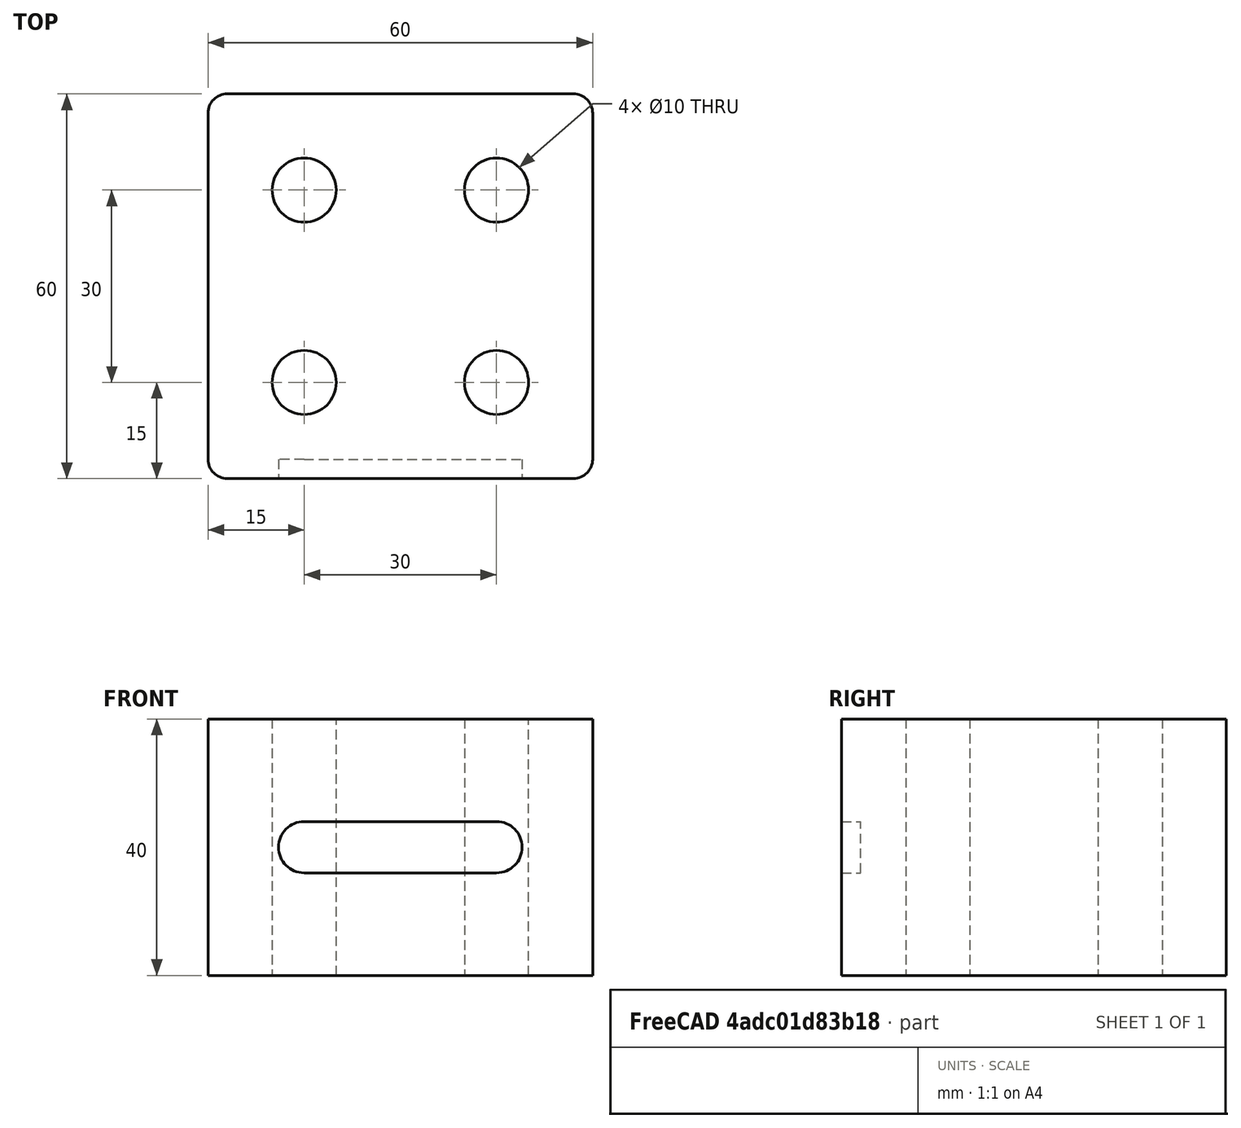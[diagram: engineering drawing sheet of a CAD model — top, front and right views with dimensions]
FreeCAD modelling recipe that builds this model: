
FCSTD DOCUMENT  (FreeCAD 1.0R39319 (Git))
Label: Assignment_10.1_Block(2d_Drawing)
License: All rights reserved
LicenseURL: https://en.wikipedia.org/wiki/All_rights_reserved
objects: TechDraw::DrawViewDimension×9, TechDraw::DrawViewAnnotation×5, TechDraw::DrawProjGroupItem×4, Sketcher::SketchObject×2, TechDraw::DrawViewBalloon×2, PartDesign::Pad×1, PartDesign::Pocket×1, PartDesign::Fillet×1, PartDesign::Body×1, TechDraw::DrawSVGTemplate×1, TechDraw::DrawProjGroup×1, TechDraw::DrawPage×1
note: 29 computed .brp shape members not serialized (recipe doc carries the construction recipe); baked Part::Feature solids carry a one-line shape summary decoded from their .brp

FEATURE [Sketcher::SketchObject] Sketch
  ArcFitTolerance = 1e-06
  AttachmentSupport = -> [XY_Plane]
  FullyConstrained = true
  MakeInternals = false
  MapMode = 5
  sketch-geometry (9):
    g0: LineSegment StartX=30 StartY=-30 StartZ=0 EndX=30 EndY=30 EndZ=0
    g1: LineSegment StartX=30 StartY=30 StartZ=0 EndX=-30 EndY=30 EndZ=0
    g2: LineSegment StartX=-30 StartY=30 StartZ=0 EndX=-30 EndY=-30 EndZ=0
    g3: LineSegment StartX=-30 StartY=-30 StartZ=0 EndX=30 EndY=-30 EndZ=0
    g4: GeomPoint [constr] X=5e-16 Y=-8e-16 Z=0
    g5: Circle CenterX=-15 CenterY=15 CenterZ=0 NormalX=0 NormalY=0 NormalZ=1 AngleXU=0 Radius=5
    g6: Circle CenterX=15 CenterY=15 CenterZ=0 NormalX=0 NormalY=0 NormalZ=1 AngleXU=0 Radius=5
    g7: Circle CenterX=-15 CenterY=-15 CenterZ=0 NormalX=0 NormalY=0 NormalZ=1 AngleXU=0 Radius=5
    g8: Circle CenterX=15 CenterY=-15 CenterZ=0 NormalX=0 NormalY=0 NormalZ=1 AngleXU=0 Radius=5
  constraints (24):
    c: Coincident(g0,g1)
    c: Coincident(g1,g2)
    c: Coincident(g2,g3)
    c: Coincident(g3,g0)
    c: Vertical(g0)
    c: Vertical(g2)
    c: Horizontal(g1)
    c: Horizontal(g3)
    c: Symmetric(g2,g0,g4)
    c: Coincident(g4,g-1)
    c: Equal(g1,g2)
    c: DistanceY(g2,g2) = 60
    c: Equal(g5,g6)
    c: Equal(g5,g8)
    c: Equal(g5,g7)
    c: Diameter(g5) = 10
    c: Horizontal(g5,g6)
    c: Vertical(g5,g7)
    c: Distance(g5,g-2) = 15
    c: Distance(g5,g-1) = 15
    c: Distance(g6,g-2) = 15
    c: Vertical(g6,g8)
    c: Horizontal(g7,g8)
    c: DistanceY(g8,g-1) = 15
FEATURE [PartDesign::Pad] Pad
  Direction = (0,0,1)
  Length = 40
  Length2 = 10
  Profile = -> Sketch
  ReferenceAxis = -> Sketch [N_Axis]
  Refine = true
  Suppressed = false
  Type = 0
FEATURE [Sketcher::SketchObject] Sketch001
  ArcFitTolerance = 1e-06
  AttachmentSupport = -> [Pad]
  FullyConstrained = true
  MakeInternals = false
  MapMode = 5
  Placement = pos=(0,-30,0) rot=(1,0,0;1.5708rad)
  sketch-geometry (4):
    g0: ArcOfCircle CenterX=-15 CenterY=20 CenterZ=0 NormalX=0 NormalY=0 NormalZ=1 AngleXU=0 Radius=4 StartAngle=1.5708 EndAngle=4.71239
    g1: ArcOfCircle CenterX=15 CenterY=20 CenterZ=0 NormalX=0 NormalY=0 NormalZ=1 AngleXU=0 Radius=4 StartAngle=4.71239 EndAngle=7.85398
    g2: LineSegment StartX=-15 StartY=24 StartZ=0 EndX=15 EndY=24 EndZ=0
    g3: LineSegment StartX=-15 StartY=16 StartZ=0 EndX=15 EndY=16 EndZ=0
  constraints (9):
    c: Tangent(g0,g2) = 1.5708
    c: Tangent(g0,g3) = -1.5708
    c: Tangent(g1,g2) = 1.5708
    c: Tangent(g1,g3) = -1.5708
    c: Equal(g0,g1)
    c: Radius(g0) = 4
    c: Symmetric(g0,g1,g-2)
    c: DistanceX(g0,g1) = 30
    c: DistanceY(g-1,g1) = 20
FEATURE [PartDesign::Pocket] Pocket
  BaseFeature = -> Pad
  Direction = (0,1,-2e-16)
  Length = 3
  Length2 = 5
  Profile = -> Sketch001
  ReferenceAxis = -> Sketch001 [N_Axis]
  Refine = true
  Suppressed = false
  Type = 0
FEATURE [PartDesign::Fillet] Fillet
  Base = -> Pocket [Edge1,Edge2,Edge5,Edge12]
  BaseFeature = -> Pocket
  Radius = 3
  Refine = true
  SupportTransform = false
  Suppressed = false
  UseAllEdges = false
FEATURE [PartDesign::Body] Body
  AllowCompound = false
  Group = -> [Sketch,Pad,Sketch001,Pocket,Fillet]
  Origin = -> Origin
  Tip = -> Fillet
FEATURE [TechDraw::DrawSVGTemplate] Template
  EditableTexts = AuthorName=REHAN K. NADAF; CheckDate=CHECK DATE; CreationDate=29-11-2025; DrawingNumber=NUMBER; FC-Title=Block(2d_Drawing); SheetNumber=1 / 1; Subtitle=Assignment_10.1_Block(2d_Drawing); SupervisorName=ProBUILD; Weight=WEIGHT; scale=1 : 1
  Height = 297
  Orientation = 1
  Template = C:/Program Files/FreeCAD 1.0/data/Mod/TechDraw/Templates/A3_Landscape_TD.svg
  Width = 420
FEATURE [TechDraw::DrawProjGroupItem] View  label="Front"
  CoarseView = false
  Direction = (0,-1,0)
  Focus = 100
  HardHidden = true
  IsoCount = 0
  IsoHidden = false
  IsoVisible = false
  LockPosition = true
  Perspective = false
  Rotation = 0
  RotationVector = (1,0,0)
  ScaleType = 2
  ScrubCount = 1
  SeamHidden = false
  SeamVisible = false
  SmoothHidden = false
  SmoothVisible = true
  Source = -> [Body]
  Type = 0
  X = 0
  XDirection = (1,0,0)
  Y = 0
FEATURE [TechDraw::DrawProjGroupItem] ProjItem  label="Top"
  CoarseView = false
  Direction = (0,0,1)
  Focus = 100
  HardHidden = false
  IsoCount = 0
  IsoHidden = false
  IsoVisible = false
  LockPosition = true
  Perspective = false
  Rotation = 0
  RotationVector = (1,0,0)
  ScaleType = 0
  ScrubCount = 1
  SeamHidden = false
  SeamVisible = false
  SmoothHidden = false
  SmoothVisible = true
  Source = -> [Body]
  Type = 4
  X = 0
  XDirection = (1,0,0)
  Y = -121.319
FEATURE [TechDraw::DrawProjGroupItem] ProjItem001  label="Left"
  CoarseView = true
  Direction = (-1,-1e-16,0)
  Focus = 100
  HardHidden = true
  IsoCount = 0
  IsoHidden = false
  IsoVisible = false
  LockPosition = true
  Perspective = false
  Rotation = 0
  RotationVector = (1,0,0)
  ScaleType = 0
  ScrubCount = 1
  SeamHidden = false
  SeamVisible = false
  SmoothHidden = true
  SmoothVisible = true
  Source = -> [Body]
  Type = 1
  X = 144.836
  XDirection = (1e-16,-1,0)
  Y = 0
FEATURE [TechDraw::DrawProjGroupItem] ProjItem002  label="FrontTopLeft"
  CoarseView = false
  Direction = (-0.57735,-0.57735,0.57735)
  Focus = 100
  HardHidden = false
  IsoCount = 0
  IsoHidden = false
  IsoVisible = false
  LockPosition = true
  Perspective = false
  Rotation = 0
  RotationVector = (1,0,0)
  ScaleType = 0
  ScrubCount = 1
  SeamHidden = false
  SeamVisible = false
  SmoothHidden = false
  SmoothVisible = true
  Source = -> [Body]
  Type = 6
  X = 245.143
  XDirection = (0.707107,-0.707107,0)
  Y = -89.4382
FEATURE [TechDraw::DrawProjGroup] ProjGroup
  Anchor = -> View
  AutoDistribute = true
  LockPosition = false
  ProjectionType = 0
  Rotation = 0
  ScaleType = 0
  Source = -> [Body]
  Views = -> [View,ProjItem,ProjItem001,ProjItem002]
  X = 116.085
  Y = 212.469
  spacingX = 20
  spacingY = 20
FEATURE [TechDraw::DrawViewDimension] Dimension003
  AngleOverride = false
  Arbitrary = false
  ArbitraryTolerances = false
  BoxCorners = (2) [(-30,-20,0),(30,20,0)]
  EqualTolerance = false
  ExtensionAngle = 0
  FormatSpec = %.2w
  FormatSpecOverTolerance = %+.2w
  FormatSpecUnderTolerance = %+.2w
  Inverted = false
  LineAngle = 0
  LockPosition = false
  MeasureType = 1
  OverTolerance = 0.3
  References2D = -> [ProjItem001]
  Rotation = 0
  ScaleType = 0
  TheoreticalExact = false
  Type = 0
  UnderTolerance = 0
  X = 45.8368
  Y = 0
FEATURE [TechDraw::DrawViewDimension] Dimension004
  AngleOverride = false
  Arbitrary = false
  ArbitraryTolerances = false
  BoxCorners = (2) [(-30,-20,-1e-07),(30,20,1e-07)]
  EqualTolerance = true
  ExtensionAngle = 0
  FormatSpec = R%.2w
  FormatSpecOverTolerance = %+.2w
  FormatSpecUnderTolerance = %+.2w
  Inverted = false
  LineAngle = 0
  LockPosition = false
  MeasureType = 1
  OverTolerance = 0
  References2D = -> [View]
  Rotation = 0
  ScaleType = 0
  TheoreticalExact = false
  Type = 4
  UnderTolerance = 0
  X = 42.5292
  Y = 31.3859
FEATURE [TechDraw::DrawViewDimension] Dimension005
  AngleOverride = false
  Arbitrary = false
  ArbitraryTolerances = false
  BoxCorners = (2) [(-30,-20,-1e-07),(30,20,1e-07)]
  EqualTolerance = true
  ExtensionAngle = 0
  FormatSpec = %.2w
  FormatSpecOverTolerance = %+.2w
  FormatSpecUnderTolerance = %+.2w
  Inverted = false
  LineAngle = 0
  LockPosition = false
  MeasureType = 1
  OverTolerance = 0
  References2D = -> [View]
  Rotation = 0
  ScaleType = 0
  TheoreticalExact = false
  Type = 0
  UnderTolerance = 0
  X = -47.1386
  Y = 36.0546
FEATURE [TechDraw::DrawViewDimension] Dimension006
  AngleOverride = false
  Arbitrary = false
  ArbitraryTolerances = false
  BoxCorners = (2) [(-30,-30,0),(30,30,0)]
  EqualTolerance = true
  ExtensionAngle = 0
  FormatSpec = R%.2w
  FormatSpecOverTolerance = %+.2w
  FormatSpecUnderTolerance = %+.2w
  Inverted = false
  LineAngle = 0
  LockPosition = false
  MeasureType = 1
  OverTolerance = 0
  References2D = -> [ProjItem]
  Rotation = 0
  ScaleType = 0
  TheoreticalExact = false
  Type = 4
  UnderTolerance = 0
  X = 43.2183
  Y = 55.1734
FEATURE [TechDraw::DrawViewDimension] Dimension007
  AngleOverride = false
  Arbitrary = false
  ArbitraryTolerances = false
  BoxCorners = (2) [(-30,-30,0),(30,30,0)]
  EqualTolerance = true
  ExtensionAngle = 0
  FormatSpec = %.2w
  FormatSpecOverTolerance = %+.2w
  FormatSpecUnderTolerance = %+.2w
  Inverted = false
  LineAngle = 0
  LockPosition = false
  MeasureType = 1
  OverTolerance = 0
  References2D = -> [ProjItem]
  Rotation = 0
  ScaleType = 0
  TheoreticalExact = false
  Type = 0
  UnderTolerance = 0
  X = 56.1117
  Y = 13.4991
FEATURE [TechDraw::DrawViewDimension] Dimension008
  AngleOverride = false
  Arbitrary = false
  ArbitraryTolerances = false
  BoxCorners = (2) [(-30,-30,0),(30,30,0)]
  EqualTolerance = true
  ExtensionAngle = 0
  FormatSpec = %.2w
  FormatSpecOverTolerance = %+.2w
  FormatSpecUnderTolerance = %+.2w
  Inverted = false
  LineAngle = 0
  LockPosition = false
  MeasureType = 1
  OverTolerance = 0
  References2D = -> [ProjItem]
  Rotation = 0
  ScaleType = 0
  TheoreticalExact = false
  Type = 0
  UnderTolerance = 0
  X = -7.19505
  Y = 47.3001
FEATURE [TechDraw::DrawViewAnnotation] Annotation
  Font = osifont
  LineSpace = 100
  LockPosition = false
  MaxWidth = -1
  Rotation = 0
  ScaleType = 0
  Text = 2D Drawing of a Block
  TextSize = 5
  TextStyle = 0
  X = 376.529
  Y = 279.457
FEATURE [TechDraw::DrawViewDimension] Dimension009
  AngleOverride = false
  Arbitrary = false
  ArbitraryTolerances = false
  BoxCorners = (2) [(-30,-20,-1e-07),(30,20,1e-07)]
  EqualTolerance = true
  ExtensionAngle = 0
  FormatSpec = %.2w
  FormatSpecOverTolerance = %+.2w
  FormatSpecUnderTolerance = %+.2w
  Inverted = false
  LineAngle = 0
  LockPosition = false
  MeasureType = 1
  OverTolerance = 0
  References2D = -> [View]
  Rotation = 0
  ScaleType = 0
  TheoreticalExact = false
  Type = 0
  UnderTolerance = 0
  X = 49.8392
  Y = -34.7741
FEATURE [TechDraw::DrawViewBalloon] Balloon
  BubbleShape = 0
  EndType = 0
  EndTypeScale = 1
  KinkLength = 5
  LockPosition = false
  OriginX = 46.7509
  OriginY = -26.9533
  Rotation = 0
  ScaleType = 0
  ShapeScale = 1
  Text = 1
  TextWrapLen = -1
  X = -1.12143
  Y = -14.078
FEATURE [TechDraw::DrawViewBalloon] Balloon001
  BubbleShape = 6
  EndType = 0
  EndTypeScale = 1
  KinkLength = 7
  LockPosition = false
  OriginX = -20
  OriginY = 15
  Rotation = 0
  ScaleType = 0
  ShapeScale = 1
  SourceView = -> ProjItem
  Text = 4 Holes of ⌀10mm
  TextWrapLen = -1
  X = -57.9342
  Y = 45.8294
FEATURE [TechDraw::DrawViewAnnotation] Annotation001
  Font = osifont
  LineSpace = 100
  LockPosition = false
  MaxWidth = -1
  Rotation = 0
  ScaleType = 0
  Text = Front View
  TextSize = 5
  TextStyle = 0
  X = 116.085
  Y = 184.598
FEATURE [TechDraw::DrawViewAnnotation] Annotation002
  Font = osifont
  LineSpace = 100
  LockPosition = false
  MaxWidth = -1
  Rotation = 0
  ScaleType = 0
  Text = Side View
  TextSize = 5
  TextStyle = 0
  X = 260.921
  Y = 186.102
FEATURE [TechDraw::DrawViewAnnotation] Annotation003
  Font = osifont
  LineSpace = 100
  LockPosition = false
  MaxWidth = -1
  Rotation = 0
  ScaleType = 0
  Text = Top View
  TextSize = 5
  TextStyle = 0
  X = 116.085
  Y = 53.649
FEATURE [TechDraw::DrawViewAnnotation] Annotation004
  Font = osifont
  LineSpace = 100
  LockPosition = false
  MaxWidth = -1
  Rotation = 0
  ScaleType = 0
  Text = Isometric View
  TextSize = 5
  TextStyle = 0
  X = 361.228
  Y = 76.5862
FEATURE [TechDraw::DrawViewDimension] Dimension
  AngleOverride = false
  Arbitrary = false
  ArbitraryTolerances = false
  BoxCorners = (2) [(-30,-20,-1e-07),(30,20,1e-07)]
  EqualTolerance = true
  ExtensionAngle = 0
  FormatSpec = %.2w
  FormatSpecOverTolerance = %+.2w
  FormatSpecUnderTolerance = %+.2w
  Inverted = false
  LineAngle = 0
  LockPosition = false
  MeasureType = 1
  OverTolerance = 0
  References2D = -> [View]
  Rotation = 0
  ScaleType = 0
  TheoreticalExact = false
  Type = 0
  UnderTolerance = 0
  X = 0
  Y = 44.5425
FEATURE [TechDraw::DrawViewDimension] Dimension010
  AngleOverride = false
  Arbitrary = false
  ArbitraryTolerances = false
  BoxCorners = (2) [(-30,-30,0),(30,30,0)]
  EqualTolerance = true
  ExtensionAngle = 0
  FormatSpec = %.2w
  FormatSpecOverTolerance = %+.2w
  FormatSpecUnderTolerance = %+.2w
  Inverted = false
  LineAngle = 0
  LockPosition = false
  MeasureType = 1
  OverTolerance = 0
  References2D = -> [ProjItem]
  Rotation = 0
  ScaleType = 0
  TheoreticalExact = false
  Type = 0
  UnderTolerance = 0
  X = -49.7765
  Y = 0
FEATURE [TechDraw::DrawPage] Page
  KeepUpdated = true
  NextBalloonIndex = 4
  ProjectionType = 0
  Template = -> Template
  Views = -> [ProjGroup,Dimension003,Dimension004,Dimension005,Dimension006,Dimension007,Dimension008,Annotation,Dimension009,Balloon,Balloon001,Annotation001,Annotation002,Annotation003,Annotation004,Dimension,Dimension010]
